# Revit family: VL2E-GP200xWSxxxE
name_source: partatom
category: Leuchten
units: mm (PartAtom-declared; Revit-internal decimal feet)

## family parameters
Basisbauteil = Fläche
Beim Laden mit Abzugskörper schneiden = Nein
Bemaßung runder Anschluss = Durchmesser verwenden
Beschriftungsausrichtung beibehalten = Nein
Gemeinsam genutzt = Nein
Lichtquelle = Ja
OmniClass-Nummer = 23.80.70.11
OmniClass-Titel = Luminaries for Internal Lighting
Raumberechnungspunkt = Nein
Teiletyp = Normal

## types (7) — shared parameters
Baugruppenkennzeichen = D5020200
Datei für fotometrisches Netz = Master_VL1GP1486-5RFWS840E0900.IES
Emissionsform beim Rendern sichtbar = Nein
Farbfilter = 16777215
Farbtemperaturverschiebung bei Dämpfen der Lampe = <Keine Auswahl>
Hersteller = RIDI Leuchten GmbH
Lampe = LED
Neigungswinkel = 90.00°
URL = www.ridi.de
Von Breite des Rechtecks ausssenden = 1979 mm  [stored 6.49278 ft]
Von Länge des Rechtecks aussenden = 61 mm  [stored 0.200131 ft]
brand = RIDI
conformity mark = CE
electrical safety class = 1
height = 64 mm  [stored 0.209974 ft]
ingress protection (IP) code = IP20
length = 2000 mm  [stored 6.56168 ft]
nominal frequency = 50-60Hz
nominal voltage = 230
voltage type (AC, DC, UC) = AC
width = 67 mm
zero-valued in all types: Vorgabe-Ansicht

## per-type parameters (varying)
| type | Modell | Scheinlast | rated input power | weight |
| VL2E-GP200-5FLWS840E1300 | 2550018 | 82 VA | 82 | 2.1 kg |
| VL2E-GP200-7DAWS840E1300 | 2560018 | 84 VA | 84 | 2.1 kg |
| VL2E-GP200-13DAWS840E1300-ED | 2560018//381 | 84 VA | 84 | 2.8 kg |
| VL2E-GP200-7DAWS840E1100 | 2560215 | 65 VA | 65 | 2.1 kg |
| VL2E-GP200-7DAWS840E1200 | 2560216 | 75 VA | 75 | 2.1 kg |
| VL2E-GP200-7DAWS840E1400 | 2560203 | 92 VA | 92 | 2.1 kg |
| VL2E-GP200-7FLWS840E1300-ED | 2550018//377 | 82 VA | 82 | 2.8 kg |

note: column(s) folded — value = type name in every type: product name

note: [stored X ft] marks values corroborated as IEEE doubles in the binary element streams (Revit-internal decimal feet)
